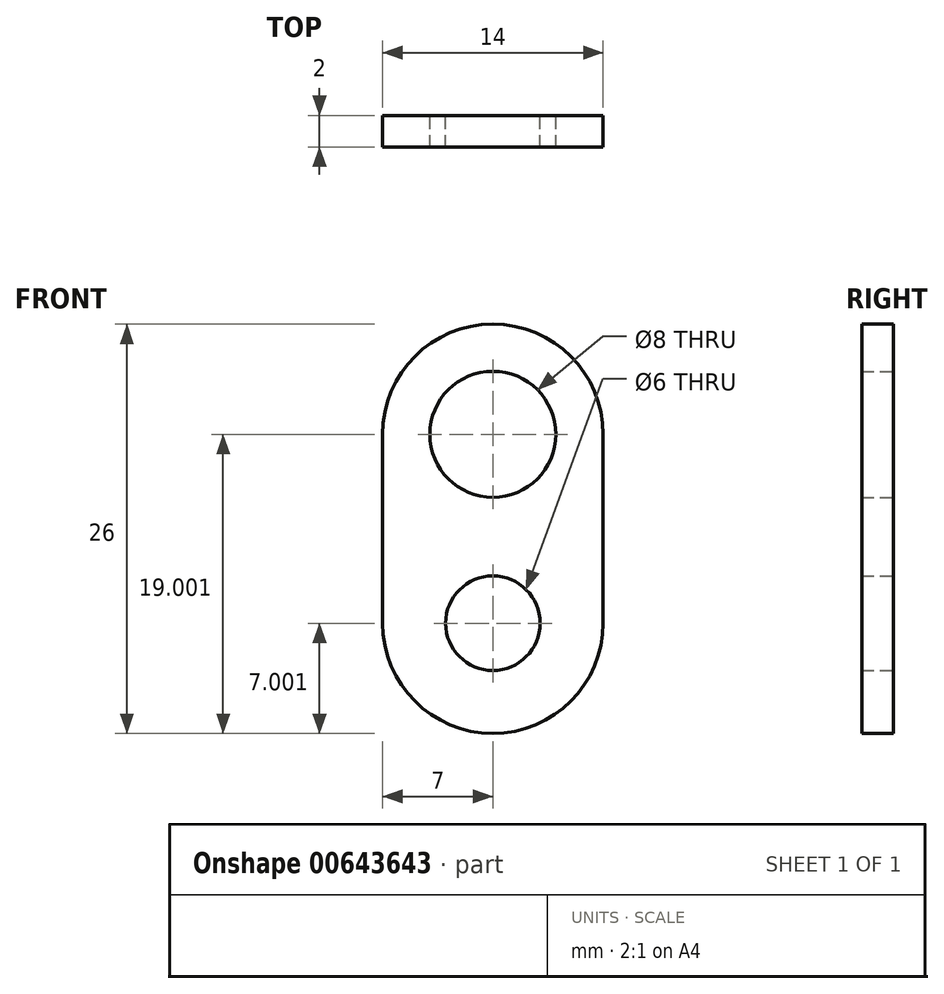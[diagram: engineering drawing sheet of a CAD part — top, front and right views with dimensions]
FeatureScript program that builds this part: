
annotation { "Feature Type Name" : "Feature", "Feature Type Description" : "" }
export const myFeature = defineFeature(function(context is Context, id is Id, definition is map)
    precondition{}
    {
        {
            var Q0;
            Q0=qCreatedBy(makeId("Front.planeOp"),FACE);
            var sketch = newSketch(context, id + "F0", { "sketchPlane" : qUnion([Q0])});
            skArc(sketch, "E0", {"start": v(7, 4.02) * mm, "mid": v(0, 11.02) * mm, "end": v(-7, 4.02) * mm});
            skArc(sketch, "E1", {"start": v(-7, -7.98) * mm, "mid": v(0, -14.98) * mm, "end": v(7, -7.98) * mm});
            skLineSegment(sketch, "E2", {"start": v(-7, -7.98) * mm, "end": v(-7, 4.02) * mm});
            skLineSegment(sketch, "E3", {"start": v(7, -7.98) * mm, "end": v(7, 4.02) * mm});
            skCircle(sketch, "E4", {"center": v(0, 4.02) * mm, "radius": 4 * mm});
            skCircle(sketch, "E5", {"center": v(0, -7.98) * mm, "radius": 3 * mm});
            skSolve(sketch);
        }
        {
            var Q0;
            Q0 = qSketchRegion(id + "F0", true);
            extrude(context, id + "F1", {"entities" : qUnion([Q0]), "depth" : 2 * mm, "offsetDistance" : 25 * mm});
        }
    });
